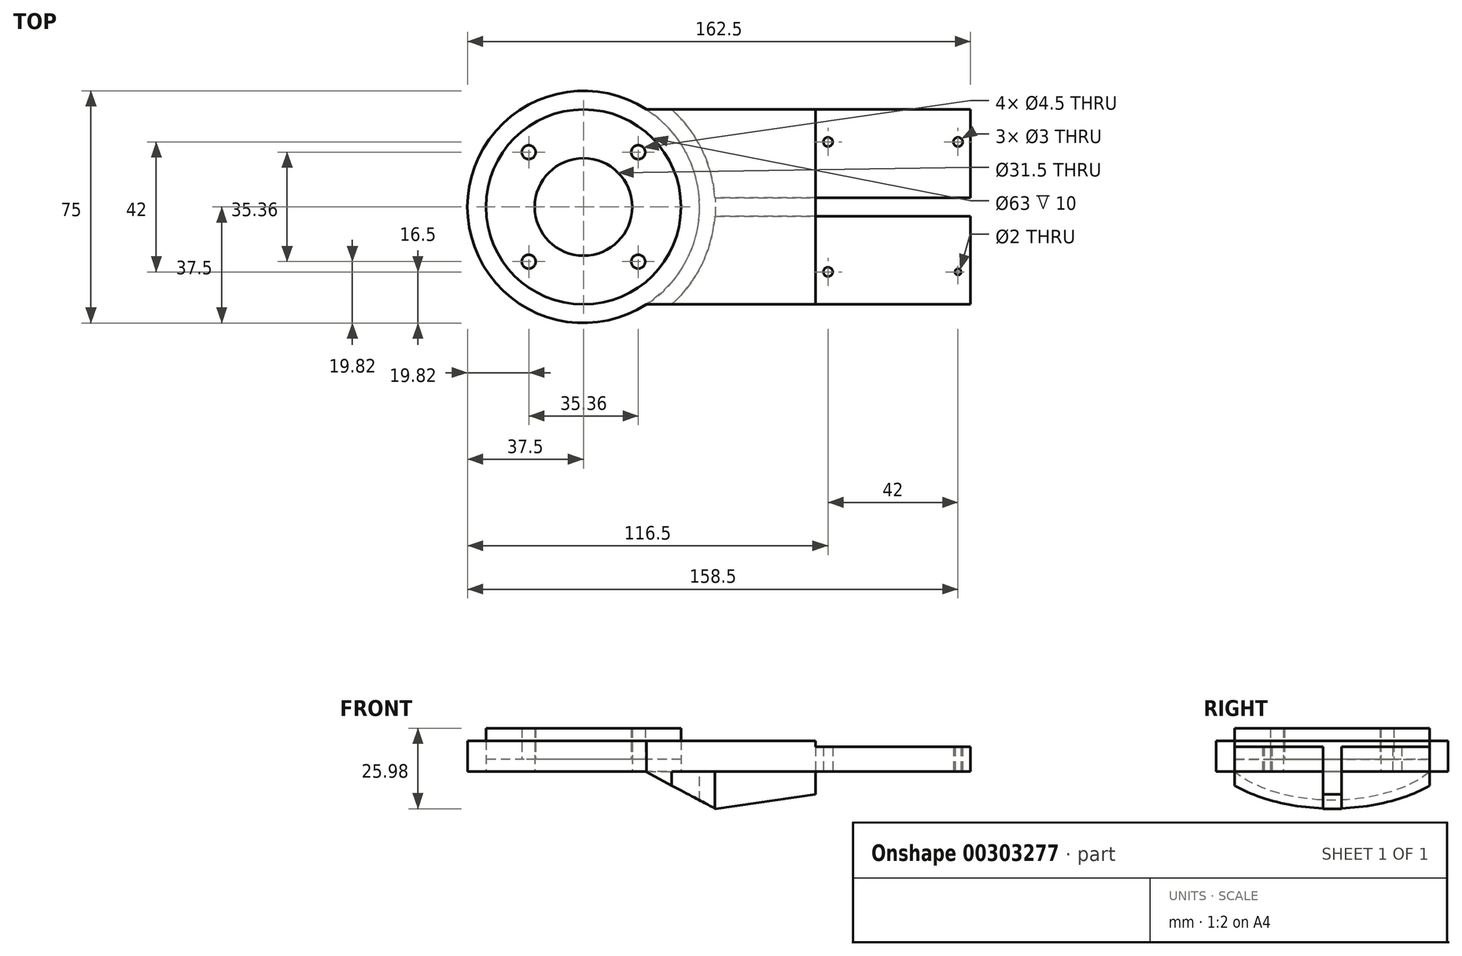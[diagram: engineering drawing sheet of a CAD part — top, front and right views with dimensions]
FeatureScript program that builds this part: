
annotation { "Feature Type Name" : "Feature", "Feature Type Description" : "" }
export const myFeature = defineFeature(function(context is Context, id is Id, definition is map)
    precondition{}
    {
        {
            var Q0;
            Q0=qCreatedBy(makeId("Top.planeOp"),FACE);
            var sketch = newSketch(context, id + "F0", { "sketchPlane" : qUnion([Q0])});
            skLineSegment(sketch, "E0.bottom", {"start": v(62.5, -31.5) * mm, "end": v(-62.5, -31.5) * mm});
            skLineSegment(sketch, "E0.top", {"start": v(62.5, 31.5) * mm, "end": v(-62.5, 31.5) * mm});
            skLineSegment(sketch, "E0.left", {"start": v(62.5, -31.5) * mm, "end": v(62.5, 31.5) * mm});
            skPoint(sketch, "E0.middle", {"position": v(0, 0) * mm});
            skArc(sketch, "E1", {"start": v(-62.5, 31.5) * mm, "mid": v(-94, 0) * mm, "end": v(-62.5, -31.5) * mm});
            skCircle(sketch, "E2", {"center": v(-80.18, -17.68) * mm, "radius": 2.25 * mm});
            skCircle(sketch, "E3", {"center": v(-44.82, -17.68) * mm, "radius": 2.25 * mm});
            skCircle(sketch, "E4", {"center": v(-44.82, 17.68) * mm, "radius": 2.25 * mm});
            skCircle(sketch, "E5", {"center": v(-80.18, 17.68) * mm, "radius": 2.25 * mm});
            skCircle(sketch, "E6", {"center": v(-62.5, 0) * mm, "radius": 15.75 * mm});
            skLineSegment(sketch, "E7", {"start": v(12.5, 31.5) * mm, "end": v(12.5, -31.5) * mm});
            skCircle(sketch, "E8", {"center": v(58.5, 21) * mm, "radius": 1.5 * mm});
            skCircle(sketch, "E9", {"center": v(16.5, 21) * mm, "radius": 1.5 * mm});
            skCircle(sketch, "E10", {"center": v(16.5, -21) * mm, "radius": 1.5 * mm});
            skCircle(sketch, "E11", {"center": v(58.5, -21) * mm, "radius": 1 * mm});
            skCircle(sketch, "E12", {"center": v(-62.5, 0) * mm, "radius": 37.5 * mm});
            skArc(sketch, "E13", {"start": v(-62.5, -31.5) * mm, "mid": v(-31, 0) * mm, "end": v(-62.5, 31.5) * mm});
            skCircle(sketch, "E14", {"center": v(-62.5, 0) * mm, "radius": 42.5 * mm});
            skLineSegment(sketch, "E15", {"start": v(62.5, 0) * mm, "end": v(62.5, -3) * mm});
            skLineSegment(sketch, "E16", {"start": v(62.5, 0) * mm, "end": v(62.5, 3) * mm});
            skLineSegment(sketch, "E17", {"start": v(62.5, 3) * mm, "end": v(-20.1, 3) * mm});
            skLineSegment(sketch, "E18", {"start": v(62.5, -3) * mm, "end": v(-20.1, -3) * mm});
            skSolve(sketch);
        }
        {
            var Q0;
            {var subQ0=sQuery(id+"F0.wireOp",EDGE,"E7");var subQ1=sQuery(id+"F0.wireOp",EDGE,"E0.top");var subQ2=makeQuery(id+"F0.imprint","INTERSECT",VERTEX,{"derivedFrom":[subQ1,subQ0]});Q0=makeQuery(id+"F0.imprint","IMPRINT",FACE,{"disambiguationData":[TD([[makeQuery(id+"F0.imprint","IMPRINT",EDGE,{"disambiguationData":[TD([[subQ2,-1.0]])],"derivedFrom":subQ1}),1.0]])]});}
            var Q1;
            {var subQ0=sQuery(id+"F0.wireOp",EDGE,"E7");var subQ1=sQuery(id+"F0.wireOp",EDGE,"E0.bottom");var subQ2=makeQuery(id+"F0.imprint","INTERSECT",VERTEX,{"derivedFrom":[subQ1,subQ0]});Q1=makeQuery(id+"F0.imprint","IMPRINT",FACE,{"disambiguationData":[TD([[makeQuery(id+"F0.imprint","IMPRINT",EDGE,{"disambiguationData":[TD([[subQ2,-1.0]])],"derivedFrom":subQ1}),-1.0]])]});}
            var Q2;
            {var subQ0=sQuery(id+"F0.wireOp",EDGE,"E17");var subQ1=sQuery(id+"F0.wireOp",EDGE,"E7");var subQ2=makeQuery(id+"F0.imprint","INTERSECT",VERTEX,{"derivedFrom":[subQ1,subQ0]});Q2=makeQuery(id+"F0.imprint","IMPRINT",FACE,{"disambiguationData":[TD([[makeQuery(id+"F0.imprint","IMPRINT",EDGE,{"disambiguationData":[TD([[subQ2,-1.0]])],"derivedFrom":subQ1}),-1.0]])]});}
            var Q3;
            {var subQ0=sQuery(id+"F0.wireOp",EDGE,"E13");Q3=makeQuery(id+"F0.imprint","IMPRINT",FACE,{"disambiguationData":[TD([[makeQuery(id+"F0.imprint","IMPRINT",EDGE,{"derivedFrom":subQ0}),-1.0]])]});}
            var Q4;
            Q4=makeQuery(id+"F0.imprint","IMPRINT",FACE,{"disambiguationData":[TD([[makeQuery(id+"F0.imprint","IMPRINT",EDGE,{"derivedFrom":sQuery(id+"F0.wireOp",EDGE,"E6")}),1.0]])]});
            var Q5;
            {var subQ1=sQuery(id+"F0.wireOp",EDGE,"E1");Q5=makeQuery(id+"F0.imprint","IMPRINT",FACE,{"disambiguationData":[TD([[makeQuery(id+"F0.imprint","IMPRINT",EDGE,{"derivedFrom":subQ1}),-1.0]])]});}
            var Q6;
            {var subQ1=sQuery(id+"F0.wireOp",EDGE,"E0.bottom");var subQ5=sQuery(id+"F0.wireOp",EDGE,"E14");var subQ6=makeQuery(id+"F0.imprint","INTERSECT",VERTEX,{"derivedFrom":[subQ1,subQ5]});Q6=makeQuery(id+"F0.imprint","IMPRINT",FACE,{"disambiguationData":[TD([[makeQuery(id+"F0.imprint","IMPRINT",EDGE,{"disambiguationData":[TD([[subQ6,-1.0]])],"derivedFrom":subQ1}),-1.0]])]});}
            extrude(context, id + "F1", {"entities" : qUnion([Q0, Q1, Q2, Q3, Q4, Q5, Q6]), "depth" : 10 * mm, "offsetDistance" : 25 * mm});
        }
        {
            var Q0;
            Q0=makeQuery(id+"F0.imprint","IMPRINT",FACE,{"disambiguationData":[TD([[makeQuery(id+"F0.imprint","IMPRINT",EDGE,{"derivedFrom":sQuery(id+"F0.wireOp",EDGE,"E8")}),-1.0]])]});
            var Q1;
            {var subQ1=sQuery(id+"F0.wireOp",EDGE,"E15");Q1=makeQuery(id+"F0.imprint","IMPRINT",FACE,{"disambiguationData":[TD([[makeQuery(id+"F0.imprint","IMPRINT",EDGE,{"derivedFrom":subQ1}),-1.0]])]});}
            var Q2;
            Q2=makeQuery(id+"F0.imprint","IMPRINT",FACE,{"disambiguationData":[TD([[makeQuery(id+"F0.imprint","IMPRINT",EDGE,{"derivedFrom":sQuery(id+"F0.wireOp",EDGE,"E10")}),-1.0]])]});
            extrude(context, id + "F2", {"entities" : qUnion([Q0, Q1, Q2]), "operationType" : NewBodyOperationType.ADD, "depth" : 8 * mm, "offsetDistance" : 25 * mm});
        }
        {
            var Q0;
            Q0=makeQuery(id+"F0.imprint","IMPRINT",FACE,{"disambiguationData":[TD([[makeQuery(id+"F0.imprint","IMPRINT",EDGE,{"derivedFrom":sQuery(id+"F0.wireOp",EDGE,"E1")}),1.0]])]});
            extrude(context, id + "F3", {"entities" : qUnion([Q0]), "depth" : 14 * mm, "offsetDistance" : 25 * mm, "hasSecondDirection" : true, "secondDirectionOppositeDirection" : false, "secondDirectionDepth" : 4 * mm});
        }
        {
            var Q0;
            {var subQ1=sQuery(id+"F0.wireOp",EDGE,"E0.bottom");var subQ5=sQuery(id+"F0.wireOp",EDGE,"E14");var subQ6=makeQuery(id+"F0.imprint","INTERSECT",VERTEX,{"derivedFrom":[subQ1,subQ5]});Q0=makeQuery(id+"F0.imprint","IMPRINT",FACE,{"disambiguationData":[TD([[makeQuery(id+"F0.imprint","IMPRINT",EDGE,{"disambiguationData":[TD([[subQ6,-1.0]])],"derivedFrom":subQ1}),-1.0]])]});}
            var Q1;
            {var subQ0=sQuery(id+"F0.wireOp",EDGE,"E17");var subQ1=sQuery(id+"F0.wireOp",EDGE,"E7");var subQ2=makeQuery(id+"F0.imprint","INTERSECT",VERTEX,{"derivedFrom":[subQ1,subQ0]});Q1=makeQuery(id+"F0.imprint","IMPRINT",FACE,{"disambiguationData":[TD([[makeQuery(id+"F0.imprint","IMPRINT",EDGE,{"disambiguationData":[TD([[subQ2,-1.0]])],"derivedFrom":subQ1}),-1.0]])]});}
            var Q2;
            {var subQ1=sQuery(id+"F0.wireOp",EDGE,"E15");Q2=makeQuery(id+"F0.imprint","IMPRINT",FACE,{"disambiguationData":[TD([[makeQuery(id+"F0.imprint","IMPRINT",EDGE,{"derivedFrom":subQ1}),-1.0]])]});}
            extrude(context, id + "F4", {"entities" : qUnion([Q0, Q1, Q2]), "operationType" : NewBodyOperationType.ADD, "oppositeDirection" : true, "depth" : 12 * mm, "offsetDistance" : 25 * mm});
        }
        {
            var Q0;
            Q0=qCreatedBy(makeId("Front.planeOp"),FACE);
            var sketch = newSketch(context, id + "F5", { "sketchPlane" : qUnion([Q0])});
            skLineSegment(sketch, "E19", {"start": v(0, 0) * mm, "end": v(62.5, 0) * mm});
            skLineSegment(sketch, "E20", {"start": v(62.5, 0) * mm, "end": v(62.5, -13.68) * mm});
            skLineSegment(sketch, "E21", {"start": v(0, 0) * mm, "end": v(-19.86, 0) * mm});
            skLineSegment(sketch, "E22", {"start": v(-19.86, 0) * mm, "end": v(-19.86, -11.98) * mm});
            skLineSegment(sketch, "E23", {"start": v(-19.86, -11.98) * mm, "end": v(62.5, -13.68) * mm});
            skLineSegment(sketch, "E24", {"start": v(-19.86, 0) * mm, "end": v(-42.42, 0) * mm});
            skLineSegment(sketch, "E25", {"start": v(-42.42, 0) * mm, "end": v(-42.42, -12.11) * mm});
            skLineSegment(sketch, "E26", {"start": v(-42.42, -12.11) * mm, "end": v(-19.86, -12.11) * mm});
            skLineSegment(sketch, "E27", {"start": v(-19.86, -12.11) * mm, "end": v(-19.86, -11.98) * mm});
            skLineSegment(sketch, "E28", {"start": v(-19.86, -11.98) * mm, "end": v(-42.42, 0) * mm});
            skLineSegment(sketch, "E29", {"start": v(-19.86, -11.98) * mm, "end": v(62.5, 0) * mm});
            skLineSegment(sketch, "E30.bottom", {"start": v(62.5, 0) * mm, "end": v(-101.67, 0) * mm});
            skLineSegment(sketch, "E30.top", {"start": v(62.5, 16.26) * mm, "end": v(-101.67, 16.26) * mm});
            skLineSegment(sketch, "E30.left", {"start": v(62.5, 0) * mm, "end": v(62.5, 16.26) * mm});
            skLineSegment(sketch, "E30.right", {"start": v(-101.67, 0) * mm, "end": v(-101.67, 16.26) * mm});
            skSolve(sketch);
        }
        {
            var Q0;
            Q0=makeQuery(id+"F5.imprint","IMPRINT",FACE,{"disambiguationData":[TD([[makeQuery(id+"F5.imprint","IMPRINT",EDGE,{"derivedFrom":sQuery(id+"F5.wireOp",EDGE,"E30.top")}),1.0]])]});
            var Q1;
            {var subQ0=sQuery(id+"F5.wireOp",EDGE,"E22");Q1=makeQuery(id+"F5.imprint","IMPRINT",FACE,{"disambiguationData":[TD([[makeQuery(id+"F5.imprint","IMPRINT",EDGE,{"derivedFrom":subQ0}),-1.0]])]});}
            var Q2;
            {var subQ0=sQuery(id+"F5.wireOp",EDGE,"E22");Q2=makeQuery(id+"F5.imprint","IMPRINT",FACE,{"disambiguationData":[TD([[makeQuery(id+"F5.imprint","IMPRINT",EDGE,{"derivedFrom":subQ0}),1.0]])]});}
            extrude(context, id + "F6", {"entities" : qUnion([Q0, Q1, Q2]), "operationType" : NewBodyOperationType.INTERSECT, "endBound" : BoundingType.SYMMETRIC, "depth" : 75 * mm, "offsetDistance" : 25 * mm});
        }
    });
